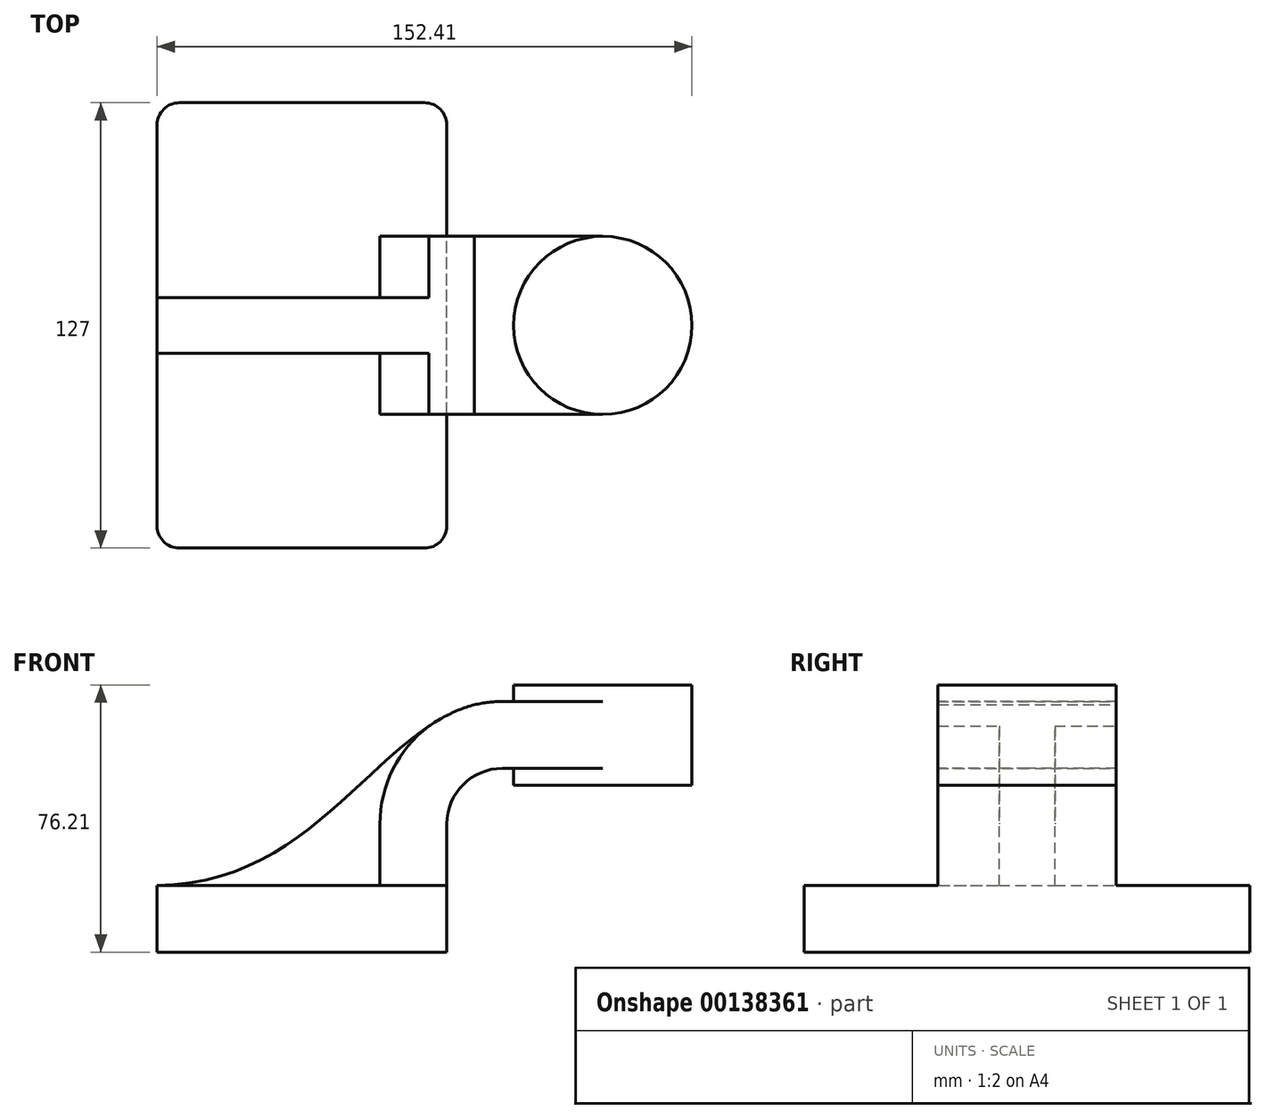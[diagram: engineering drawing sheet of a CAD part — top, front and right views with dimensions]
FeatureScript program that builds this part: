
annotation { "Feature Type Name" : "Feature", "Feature Type Description" : "" }
export const myFeature = defineFeature(function(context is Context, id is Id, definition is map)
    precondition{}
    {
        {
            var Q0;
            Q0=qCreatedBy(makeId("Front.planeOp"),FACE);
            var sketch = newSketch(context, id + "F0", { "sketchPlane" : qUnion([Q0])});
            skLineSegment(sketch, "E0.bottom", {"start": v(-41.28, -9.53) * mm, "end": v(41.28, -9.53) * mm});
            skLineSegment(sketch, "E0.top", {"start": v(-41.28, 9.52) * mm, "end": v(41.28, 9.52) * mm});
            skLineSegment(sketch, "E0.left", {"start": v(-41.28, -9.53) * mm, "end": v(-41.28, 9.53) * mm});
            skLineSegment(sketch, "E0.right", {"start": v(41.28, -9.53) * mm, "end": v(41.28, 9.52) * mm});
            skPoint(sketch, "E0.middle", {"position": v(0, 0) * mm});
            skLineSegment(sketch, "E1.bottom", {"start": v(60.32, 38.1) * mm, "end": v(111.12, 38.1) * mm});
            skLineSegment(sketch, "E1.top", {"start": v(60.32, 66.67) * mm, "end": v(111.12, 66.67) * mm});
            skLineSegment(sketch, "E1.left", {"start": v(60.32, 38.1) * mm, "end": v(60.32, 66.67) * mm});
            skLineSegment(sketch, "E1.right", {"start": v(111.12, 38.1) * mm, "end": v(111.12, 66.67) * mm});
            skPoint(sketch, "E1.middle", {"position": v(85.72, 52.39) * mm});
            skLineSegment(sketch, "E2", {"start": v(41.27, 9.52) * mm, "end": v(41.27, 27) * mm});
            skArc(sketch, "E3", {"start": v(41.27, 27) * mm, "mid": v(45.92, 38.23) * mm, "end": v(57.15, 42.88) * mm});
            skArc(sketch, "E4.1", {"start": v(22.23, 27) * mm, "mid": v(32.45, 51.7) * mm, "end": v(57.15, 61.93) * mm});
            skLineSegment(sketch, "E4.2", {"start": v(22.22, 9.52) * mm, "end": v(22.22, 27) * mm});
            skLineSegment(sketch, "E5", {"start": v(57.15, 42.88) * mm, "end": v(85.72, 42.88) * mm});
            skLineSegment(sketch, "E6", {"start": v(57.15, 61.93) * mm, "end": v(85.72, 61.93) * mm});
            skLineSegment(sketch, "E7", {"start": v(85.72, 42.88) * mm, "end": v(85.72, 61.93) * mm});
            skLineSegment(sketch, "E8", {"start": v(85.72, 42.88) * mm, "end": v(85.72, 38.1) * mm});
            skLineSegment(sketch, "E9", {"start": v(85.72, 61.93) * mm, "end": v(85.72, 66.67) * mm});
            skFitSpline(sketch, "E10", {"points": [v(-41.28, 9.53) * mm, v(57.15, 61.93) * mm], "startDerivative": vector(147.28, 0) * mm, "endDerivative": vector(98.44, -1.84) * mm});
            skSolve(sketch);
        }
        {
            var Q0;
            Q0=makeQuery(id+"F0.imprint","IMPRINT",FACE,{"disambiguationData":[TD([[makeQuery(id+"F0.imprint","IMPRINT",EDGE,{"derivedFrom":sQuery(id+"F0.wireOp",EDGE,"E0.bottom")}),1.0]])]});
            extrude(context, id + "F1", {"entities" : qUnion([Q0]), "endBound" : BoundingType.SYMMETRIC, "depth" : 127 * mm});
        }
        {
            var Q0;
            {var subQ2=sQuery(id+"F0.wireOp",EDGE,"E2");Q0=makeQuery(id+"F0.imprint","IMPRINT",FACE,{"disambiguationData":[TD([[makeQuery(id+"F0.imprint","IMPRINT",EDGE,{"derivedFrom":subQ2}),1.0]])]});}
            var Q1;
            {var subQ5=sQuery(id+"F0.wireOp",EDGE,"E7");Q1=makeQuery(id+"F0.imprint","IMPRINT",FACE,{"disambiguationData":[TD([[makeQuery(id+"F0.imprint","IMPRINT",EDGE,{"derivedFrom":subQ5}),1.0]])]});}
            extrude(context, id + "F2", {"entities" : qUnion([Q0, Q1]), "operationType" : NewBodyOperationType.ADD, "endBound" : BoundingType.SYMMETRIC, "depth" : 50.8 * mm});
        }
        {
            var Q0;
            {var subQ3=sQuery(id+"F0.wireOp",EDGE,"E4.2");Q0=makeQuery(id+"F0.imprint","IMPRINT",FACE,{"disambiguationData":[TD([[makeQuery(id+"F0.imprint","IMPRINT",EDGE,{"derivedFrom":subQ3}),1.0]])]});}
            extrude(context, id + "F3", {"entities" : qUnion([Q0]), "operationType" : NewBodyOperationType.ADD, "endBound" : BoundingType.SYMMETRIC, "depth" : 15.88 * mm});
        }
        {
            var Q0;
            {var subQ0=sQuery(id+"F0.wireOp",EDGE,"E1.right");Q0=makeQuery(id+"F0.imprint","IMPRINT",FACE,{"disambiguationData":[TD([[makeQuery(id+"F0.imprint","IMPRINT",EDGE,{"derivedFrom":subQ0}),1.0]])]});}
            var Q1;
            Q1=sQuery(id+"F0.wireOp",EDGE,"E7");
            revolve(context, id + "F4", {"operationType" : NewBodyOperationType.ADD, "entities" : qUnion([Q0]), "axis" : qUnion([Q1]), "revolveType" : RevolveType.FULL});
        }
        {
            var Q0;
            Q0=makeQuery(id+"F1.opExtrude","CAP_EDGE",EDGE,{"disambiguationData":[OSD([sQuery(id+"F0.wireOp",EDGE,"E0.left")])],"isStart":false});
            var Q1;
            Q1=makeQuery(id+"F1.opExtrude","CAP_EDGE",EDGE,{"disambiguationData":[OSD([sQuery(id+"F0.wireOp",EDGE,"E0.right")])],"isStart":false});
            var Q2;
            Q2=makeQuery(id+"F1.opExtrude","CAP_EDGE",EDGE,{"disambiguationData":[OSD([sQuery(id+"F0.wireOp",EDGE,"E0.left")])],"isStart":true});
            var Q3;
            Q3=makeQuery(id+"F1.opExtrude","CAP_EDGE",EDGE,{"disambiguationData":[OSD([sQuery(id+"F0.wireOp",EDGE,"E0.right")])],"isStart":true});
            fillet(context, id + "F5", {"entities" : qUnion([Q0, Q1, Q2, Q3]), "radius" : 6.35 * mm, "tangentPropagation" : true, "allowEdgeOverflow" : false});
        }
    });
